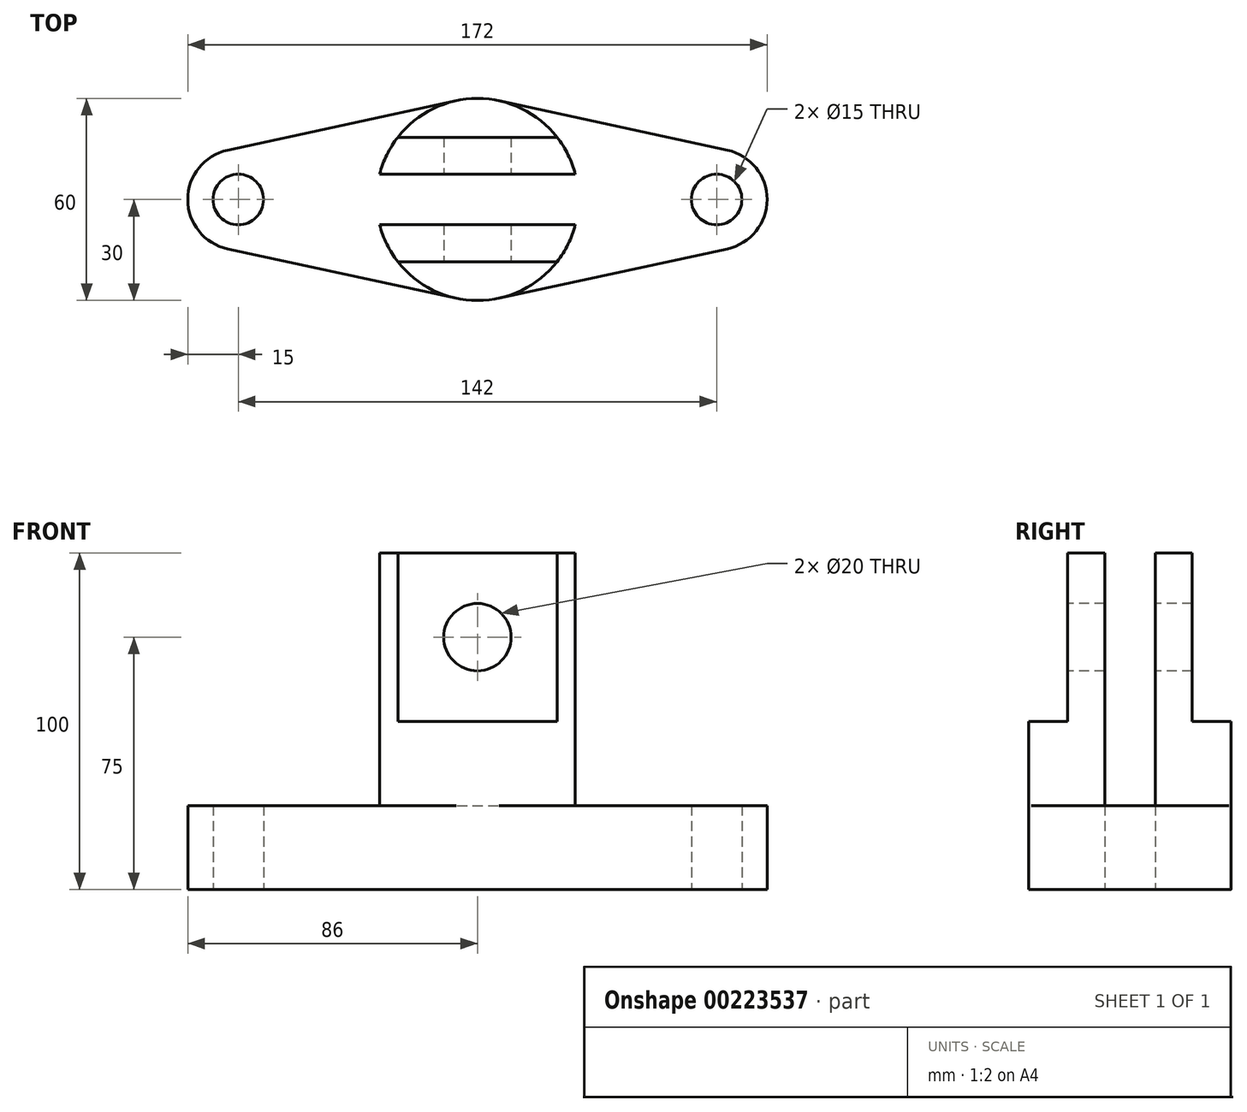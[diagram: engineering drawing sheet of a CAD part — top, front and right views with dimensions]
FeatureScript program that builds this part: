
annotation { "Feature Type Name" : "Feature", "Feature Type Description" : "" }
export const myFeature = defineFeature(function(context is Context, id is Id, definition is map)
    precondition{}
    {
        {
            var Q0;
            Q0=qCreatedBy(makeId("Top.planeOp"),FACE);
            var sketch = newSketch(context, id + "F0", { "sketchPlane" : qUnion([Q0])});
            skCircle(sketch, "E0", {"center": v(-71, 0) * mm, "radius": 7.5 * mm});
            skLineSegment(sketch, "E1", {"start": v(0, 54.52) * mm, "end": v(0, -45.04) * mm, "construction": true});
            skCircle(sketch, "E2", {"center": v(-71, 0) * mm, "radius": 15 * mm});
            skCircle(sketch, "E3", {"center": v(0, 0) * mm, "radius": 30 * mm});
            skLineSegment(sketch, "E4", {"start": v(-74.17, 14.66) * mm, "end": v(-6.34, 29.32) * mm});
            skLineSegment(sketch, "E5", {"start": v(-74.17, -14.66) * mm, "end": v(-6.34, -29.32) * mm});
            skLineSegment(sketch, "E6.MirrorCS", {"start": v(74.17, 14.66) * mm, "end": v(6.34, 29.32) * mm});
            skLineSegment(sketch, "E7.MirrorCS", {"start": v(74.17, -14.66) * mm, "end": v(6.34, -29.32) * mm});
            skCircle(sketch, "E8.MirrorC", {"center": v(71, 0) * mm, "radius": 15 * mm});
            skCircle(sketch, "E9.MirrorC", {"center": v(71, 0) * mm, "radius": 7.5 * mm});
            skSolve(sketch);
        }
        {
            var Q0;
            Q0=qSketchRegion(id+"F0",true);
            extrude(context, id + "F1", {"entities" : qUnion([Q0]), "depth" : 25 * mm});
        }
        {
            var Q0;
            {var subQ0=sQuery(id+"F0.wireOp",EDGE,"E3");var subQ1=makeQuery(id+"F0.imprint","INTERSECT",VERTEX,{"derivedFrom":[subQ0,sQuery(id+"F0.wireOp",EDGE,"E4")]});Q0=makeQuery(id+"F0.imprint","IMPRINT",FACE,{"disambiguationData":[TD([[makeQuery(id+"F0.imprint","IMPRINT",EDGE,{"disambiguationData":[TD([[subQ1,1.0]])],"derivedFrom":subQ0}),1.0]])]});}
            extrude(context, id + "F2", {"entities" : qUnion([Q0]), "operationType" : NewBodyOperationType.ADD, "depth" : 100 * mm});
        }
        {
            var Q0;
            Q0=makeQuery(id+"F2.opExtrude","CAP_FACE",FACE,{"disambiguationData":[OSD([sQuery(id+"F0.wireOp",EDGE,"E3")])],"isStart":false});
            var sketch = newSketch(context, id + "F3", { "sketchPlane" : qUnion([Q0])});
            skLineSegment(sketch, "E10.bottom", {"start": v(40, 7.5) * mm, "end": v(-40, 7.5) * mm});
            skLineSegment(sketch, "E10.top", {"start": v(40, -7.5) * mm, "end": v(-40, -7.5) * mm});
            skLineSegment(sketch, "E10.left", {"start": v(40, 7.5) * mm, "end": v(40, -7.5) * mm});
            skLineSegment(sketch, "E10.right", {"start": v(-40, 7.5) * mm, "end": v(-40, -7.5) * mm});
            skPoint(sketch, "E10.middle", {"position": v(0, 0) * mm});
            skSolve(sketch);
        }
        {
            var Q0;
            Q0=qSketchRegion(id+"F3",true);
            var Q1;
            {var subQ0=sQuery(id+"F0.wireOp",EDGE,"E7.MirrorCS");var subQ1=sQuery(id+"F0.wireOp",EDGE,"E6.MirrorCS");var subQ2=sQuery(id+"F0.wireOp",EDGE,"E5");var subQ3=sQuery(id+"F0.wireOp",EDGE,"E3");var subQ4=sQuery(id+"F0.wireOp",EDGE,"E4");var subQ5=sQuery(id+"F0.wireOp",EDGE,"E8.MirrorC");var subQ6=sQuery(id+"F0.wireOp",EDGE,"E9.MirrorC");Q1=makeQuery(id+"F2.boolean.opBoolean","SPLIT",FACE,{"disambiguationData":[TD([makeQuery(id+"F1.opExtrude","SWEPT_FACE",FACE,{"disambiguationData":[OSD([subQ1])]})])],"derivedFrom":makeQuery(id+"F1.opExtrude","CAP_FACE",FACE,{"disambiguationData":[OSD([sQuery(id+"F0.wireOp",EDGE,"E0"),sQuery(id+"F0.wireOp",EDGE,"E2"),subQ3,subQ4,subQ2,subQ1,subQ0,subQ5,subQ6])],"isStart":false})});}
            extrude(context, id + "F4", {"entities" : qUnion([Q0]), "operationType" : NewBodyOperationType.REMOVE, "endBound" : BoundingType.UP_TO_SURFACE, "oppositeDirection" : true, "endBoundEntityFace" : qUnion([Q1]), "depth" : 25 * mm});
        }
        {
            var Q0;
            {var subQ0=sQuery(id+"F0.wireOp",EDGE,"E3");Q0=makeQuery(id+"F4.boolean.opBoolean","SPLIT",FACE,{"disambiguationData":[TD([makeQuery(id+"F4.opExtrude","SWEPT_FACE",FACE,{"disambiguationData":[OSD([sQuery(id+"F3.wireOp",EDGE,"E10.top")])]})])],"derivedFrom":makeQuery(id+"F2.opExtrude","CAP_FACE",FACE,{"disambiguationData":[OSD([subQ0])],"isStart":false})});}
            var sketch = newSketch(context, id + "F5", { "sketchPlane" : qUnion([Q0])});
            skLineSegment(sketch, "E11.bottom", {"start": v(50, -18.5) * mm, "end": v(-50, -18.5) * mm});
            skLineSegment(sketch, "E11.top", {"start": v(50, 18.5) * mm, "end": v(-50, 18.5) * mm});
            skLineSegment(sketch, "E11.left", {"start": v(50, -18.5) * mm, "end": v(50, 18.5) * mm});
            skLineSegment(sketch, "E11.right", {"start": v(-50, -18.5) * mm, "end": v(-50, 18.5) * mm});
            skPoint(sketch, "E11.middle", {"position": v(0, 0) * mm});
            skLineSegment(sketch, "E12.bottom", {"start": v(65, -35) * mm, "end": v(-65, -35) * mm});
            skLineSegment(sketch, "E12.top", {"start": v(65, 35) * mm, "end": v(-65, 35) * mm});
            skLineSegment(sketch, "E12.left", {"start": v(65, -35) * mm, "end": v(65, 35) * mm});
            skLineSegment(sketch, "E12.right", {"start": v(-65, -35) * mm, "end": v(-65, 35) * mm});
            skSolve(sketch);
        }
        {
            var Q0;
            Q0=qSketchRegion(id+"F5",true);
            extrude(context, id + "F6", {"entities" : qUnion([Q0]), "operationType" : NewBodyOperationType.REMOVE, "oppositeDirection" : true, "depth" : 50 * mm});
        }
        {
            var Q0;
            Q0=qCreatedBy(makeId("Front.planeOp"),FACE);
            var sketch = newSketch(context, id + "F7", { "sketchPlane" : qUnion([Q0])});
            skCircle(sketch, "E13", {"center": v(0, 75) * mm, "radius": 10 * mm});
            skSolve(sketch);
        }
        {
            var Q0;
            Q0=qSketchRegion(id+"F7",true);
            extrude(context, id + "F8", {"entities" : qUnion([Q0]), "operationType" : NewBodyOperationType.REMOVE, "oppositeDirection" : true, "depth" : 50 * mm, "symmetric" : true});
        }
    });
